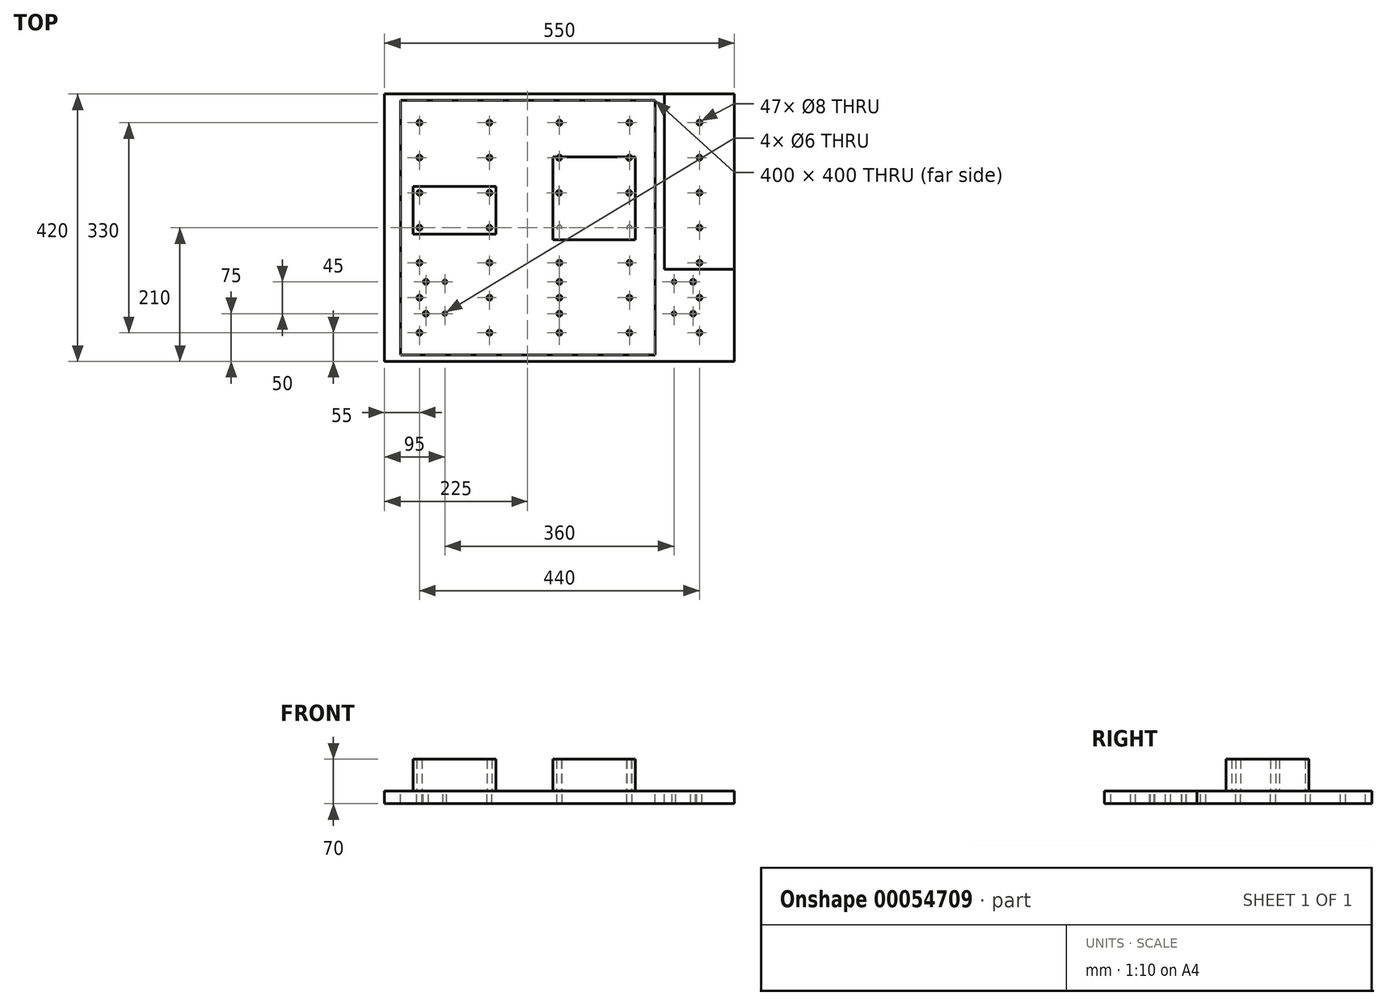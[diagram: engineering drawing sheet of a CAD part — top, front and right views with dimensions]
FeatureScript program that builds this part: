
annotation { "Feature Type Name" : "Feature", "Feature Type Description" : "" }
export const myFeature = defineFeature(function(context is Context, id is Id, definition is map)
    precondition{}
    {
        {
            var Q0;
            Q0=qCreatedBy(makeId("Top.planeOp"),FACE);
            var sketch = newSketch(context, id + "F0", { "sketchPlane" : qUnion([Q0])});
            skLineSegment(sketch, "E0.bottom", {"start": v(0, 0) * mm, "end": v(550, 0) * mm});
            skLineSegment(sketch, "E0.top", {"start": v(0, 420) * mm, "end": v(550, 420) * mm});
            skLineSegment(sketch, "E0.left", {"start": v(0, 0) * mm, "end": v(0, 420) * mm});
            skLineSegment(sketch, "E0.right", {"start": v(550, 0) * mm, "end": v(550, 420) * mm});
            skLineSegment(sketch, "E1.bottom", {"start": v(25, 10) * mm, "end": v(425, 10) * mm});
            skLineSegment(sketch, "E1.top", {"start": v(25, 410) * mm, "end": v(425, 410) * mm});
            skLineSegment(sketch, "E1.left", {"start": v(25, 10) * mm, "end": v(25, 410) * mm});
            skLineSegment(sketch, "E1.right", {"start": v(425, 10) * mm, "end": v(425, 410) * mm});
            skCircle(sketch, "E2", {"center": v(55, 45) * mm, "radius": 4 * mm});
            skCircle(sketch, "E3.0.1.0", {"center": v(55, 100) * mm, "radius": 4 * mm});
            skCircle(sketch, "E3.0.2.0", {"center": v(55, 155) * mm, "radius": 4 * mm});
            skCircle(sketch, "E3.0.3.0", {"center": v(55, 210) * mm, "radius": 4 * mm});
            skCircle(sketch, "E3.0.4.0", {"center": v(55, 265) * mm, "radius": 4 * mm});
            skCircle(sketch, "E3.0.5.0", {"center": v(55, 320) * mm, "radius": 4 * mm});
            skCircle(sketch, "E3.0.6.0", {"center": v(55, 375) * mm, "radius": 4 * mm});
            skCircle(sketch, "E3.1.0.0", {"center": v(165, 45) * mm, "radius": 4 * mm});
            skCircle(sketch, "E3.1.1.0", {"center": v(165, 100) * mm, "radius": 4 * mm});
            skCircle(sketch, "E3.1.2.0", {"center": v(165, 155) * mm, "radius": 4 * mm});
            skCircle(sketch, "E3.1.3.0", {"center": v(165, 210) * mm, "radius": 4 * mm});
            skCircle(sketch, "E3.1.4.0", {"center": v(165, 265) * mm, "radius": 4 * mm});
            skCircle(sketch, "E3.1.5.0", {"center": v(165, 320) * mm, "radius": 4 * mm});
            skCircle(sketch, "E3.1.6.0", {"center": v(165, 375) * mm, "radius": 4 * mm});
            skCircle(sketch, "E3.2.0.0", {"center": v(275, 45) * mm, "radius": 4 * mm});
            skCircle(sketch, "E3.2.1.0", {"center": v(275, 100) * mm, "radius": 4 * mm});
            skCircle(sketch, "E3.2.2.0", {"center": v(275, 155) * mm, "radius": 4 * mm});
            skCircle(sketch, "E3.2.3.0", {"center": v(275, 210) * mm, "radius": 4 * mm});
            skCircle(sketch, "E3.2.4.0", {"center": v(275, 265) * mm, "radius": 4 * mm});
            skCircle(sketch, "E3.2.5.0", {"center": v(275, 320) * mm, "radius": 4 * mm});
            skCircle(sketch, "E3.2.6.0", {"center": v(275, 375) * mm, "radius": 4 * mm});
            skCircle(sketch, "E3.3.0.0", {"center": v(385, 45) * mm, "radius": 4 * mm});
            skCircle(sketch, "E3.3.1.0", {"center": v(385, 100) * mm, "radius": 4 * mm});
            skCircle(sketch, "E3.3.2.0", {"center": v(385, 155) * mm, "radius": 4 * mm});
            skCircle(sketch, "E3.3.3.0", {"center": v(385, 210) * mm, "radius": 4 * mm});
            skCircle(sketch, "E3.3.4.0", {"center": v(385, 265) * mm, "radius": 4 * mm});
            skCircle(sketch, "E3.3.5.0", {"center": v(385, 320) * mm, "radius": 4 * mm});
            skCircle(sketch, "E3.3.6.0", {"center": v(385, 375) * mm, "radius": 4 * mm});
            skLineSegment(sketch, "E3.direction1", {"start": v(55, 45) * mm, "end": v(165, 45) * mm, "construction": true});
            skLineSegment(sketch, "E3.direction2", {"start": v(55, 45) * mm, "end": v(55, 100) * mm, "construction": true});
            skCircle(sketch, "E4.0.4.0", {"center": v(495, 45) * mm, "radius": 4 * mm});
            skCircle(sketch, "E4.0.4.1", {"center": v(495, 100) * mm, "radius": 4 * mm});
            skCircle(sketch, "E4.0.4.2", {"center": v(495, 155) * mm, "radius": 4 * mm});
            skCircle(sketch, "E4.0.4.3", {"center": v(495, 210) * mm, "radius": 4 * mm});
            skCircle(sketch, "E4.0.4.4", {"center": v(495, 265) * mm, "radius": 4 * mm});
            skCircle(sketch, "E4.0.4.5", {"center": v(495, 320) * mm, "radius": 4 * mm});
            skCircle(sketch, "E4.0.4.6", {"center": v(495, 375) * mm, "radius": 4 * mm});
            skLineSegment(sketch, "E5.bottom", {"start": v(440, 420) * mm, "end": v(550, 420) * mm});
            skLineSegment(sketch, "E5.top", {"start": v(440, 145) * mm, "end": v(550, 145) * mm});
            skLineSegment(sketch, "E5.left", {"start": v(440, 420) * mm, "end": v(440, 145) * mm});
            skLineSegment(sketch, "E5.right", {"start": v(550, 420) * mm, "end": v(550, 145) * mm});
            skCircle(sketch, "E6", {"center": v(485, 125) * mm, "radius": 4 * mm});
            skCircle(sketch, "E7", {"center": v(485, 75) * mm, "radius": 4 * mm});
            skCircle(sketch, "E8", {"center": v(65, 125) * mm, "radius": 4 * mm});
            skCircle(sketch, "E9", {"center": v(65, 75) * mm, "radius": 4 * mm});
            skCircle(sketch, "E10", {"center": v(275, 125) * mm, "radius": 4 * mm});
            skCircle(sketch, "E11", {"center": v(275, 75) * mm, "radius": 4 * mm});
            skCircle(sketch, "E12", {"center": v(95, 125) * mm, "radius": 3 * mm});
            skCircle(sketch, "E13", {"center": v(95, 75) * mm, "radius": 3 * mm});
            skCircle(sketch, "E14", {"center": v(455, 125) * mm, "radius": 3 * mm});
            skCircle(sketch, "E15", {"center": v(455, 75) * mm, "radius": 3 * mm});
            skSolve(sketch);
        }
        {
            var Q0;
            Q0=makeQuery(id+"F0.imprint","IMPRINT",FACE,{"disambiguationData":[TD([[makeQuery(id+"F0.imprint","IMPRINT",EDGE,{"derivedFrom":sQuery(id+"F0.wireOp",EDGE,"E0.bottom")}),1.0]])]});
            extrude(context, id + "F1", {"entities" : qUnion([Q0]), "oppositeDirection" : true, "depth" : 20 * mm});
        }
        {
            var Q0;
            Q0=makeQuery(id+"F0.imprint","IMPRINT",FACE,{"disambiguationData":[TD([[makeQuery(id+"F0.imprint","IMPRINT",EDGE,{"derivedFrom":sQuery(id+"F0.wireOp",EDGE,"E1.bottom")}),1.0]])]});
            var Q1;
            Q1=makeQuery(id+"F0.imprint","IMPRINT",FACE,{"disambiguationData":[TD([[makeQuery(id+"F0.imprint","IMPRINT",EDGE,{"derivedFrom":sQuery(id+"F0.wireOp",EDGE,"E4.0.4.2")}),-1.0]])]});
            extrude(context, id + "F2", {"entities" : qUnion([Q0, Q1]), "oppositeDirection" : true, "depth" : 20 * mm});
        }
        {
            var Q0;
            Q0=qCreatedBy(makeId("Top.planeOp"),FACE);
            var sketch = newSketch(context, id + "F3", { "sketchPlane" : qUnion([Q0])});
            skLineSegment(sketch, "E16.bottom", {"start": v(45, 275) * mm, "end": v(175, 275) * mm});
            skLineSegment(sketch, "E16.top", {"start": v(45, 200) * mm, "end": v(175, 200) * mm});
            skLineSegment(sketch, "E16.left", {"start": v(45, 275) * mm, "end": v(45, 200) * mm});
            skLineSegment(sketch, "E16.right", {"start": v(175, 275) * mm, "end": v(175, 200) * mm});
            skCircle(sketch, "E17.0.4.0", {"center": v(55, 265) * mm, "radius": 4 * mm});
            skCircle(sketch, "E17.0.3.0", {"center": v(55, 210) * mm, "radius": 4 * mm});
            skCircle(sketch, "E17.1.4.0", {"center": v(165, 265) * mm, "radius": 4 * mm});
            skCircle(sketch, "E17.1.3.0", {"center": v(165, 210) * mm, "radius": 4 * mm});
            skLineSegment(sketch, "E18.left", {"start": v(264.4, 321.27) * mm, "end": v(264.4, 191.27) * mm});
            skLineSegment(sketch, "E18.right", {"start": v(394.4, 321.27) * mm, "end": v(394.4, 191.27) * mm});
            skLineSegment(sketch, "E18.top", {"start": v(264.4, 191.27) * mm, "end": v(394.4, 191.27) * mm});
            skLineSegment(sketch, "E18.bottom", {"start": v(264.4, 321.27) * mm, "end": v(394.4, 321.27) * mm});
            skCircle(sketch, "E19.0.4.0", {"center": v(274.4, 319.77) * mm, "radius": 4 * mm});
            skCircle(sketch, "E19.0.3.0", {"center": v(274.4, 264.77) * mm, "radius": 4 * mm});
            skCircle(sketch, "E19.1.4.0", {"center": v(384.4, 319.77) * mm, "radius": 4 * mm});
            skCircle(sketch, "E19.1.3.0", {"center": v(384.4, 264.77) * mm, "radius": 4 * mm});
            skSolve(sketch);
        }
        {
            var Q0;
            Q0=makeQuery(id+"F3.imprint","IMPRINT",FACE,{"disambiguationData":[TD([[makeQuery(id+"F3.imprint","IMPRINT",EDGE,{"derivedFrom":sQuery(id+"F3.wireOp",EDGE,"E16.bottom")}),-1.0]])]});
            var Q1;
            {var subQ1=sQuery(id+"F3.wireOp",EDGE,"E18.left");Q1=makeQuery(id+"F3.imprint","IMPRINT",FACE,{"disambiguationData":[TD([[makeQuery(id+"F3.imprint","IMPRINT",EDGE,{"derivedFrom":subQ1}),1.0]])]});}
            extrude(context, id + "F4", {"entities" : qUnion([Q0, Q1]), "depth" : 50 * mm});
        }
    });
